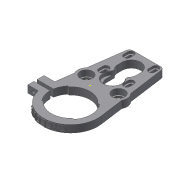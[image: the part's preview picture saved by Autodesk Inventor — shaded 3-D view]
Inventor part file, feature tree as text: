
AUTODESK INVENTOR PART (.ipt)
format: ipt  version: 2015 SP2 (Build 190223200, 223)  size: 483,840 bytes
history: native  units: mm
features: sketch x10, extrude x8, other x3, projected_geometry x3, plane x2, hole x1, pattern_linear x1, chamfer x1
ambient origin geometry x8: Origin, YZ Plane, XZ Plane, XY Plane, X Axis, Y Axis, Z Axis, Center Point
bodies: Body1 (feature_tree)
feature tree (29):
  other  "Sólido1"
  extrude  "Extrusión1"  Depth=15.45mm
  extrude  "Extrusión4"  Depth=12.0mm
  extrude  "Extrusión5"  Depth=40.0mm
  extrude  "Extrusión6"  Depth=10.0mm TaperAngle=0.0deg
  hole  "Agujero1"  [1 undecoded]
  extrude  "Extrusión8"  Depth=48.0mm
  extrude  "Extrusión10"  Depth=6.0mm
  pattern_linear  "Patrón rectangular1"  Spacing1=2.8mm  [1 undecoded]
  extrude  "Extrusión11"  Depth=1.850001mm
  sketch  "Boceto15"  dims[d29=10.0mm d30=0.0mm]
  extrude  "Extrusión12"  Depth=1.850001mm
  plane  "Plano de trabajo1"
  chamfer  "Chaflán1"  Distance=5.0mm
  plane  "Plano de trabajo6"
  sketch  "Boceto27"  dims[d43=6.235mm d44=2.8mm d45=0.0mm d46=1.850001mm d47=1.850001mm d51=5.0mm d52=5.0mm d54=34.5mm d59=5.0mm d60=5.0mm d61=1.85mm d62=15.5mm d63=4.5mm d64=9.0mm d65=0.0mm d66=20.0mm d68=31.0mm d69=20.0mm d71=31.0mm d72=8.200001mm d74=47.65mm d75=2.35mm d76=2.35mm d77=2.35mm d78=2.35mm d79=25.436099mm d80=25.436099mm d81=2.0mm d82=2.0mm d83=2.0mm d84=2.0mm d85=2.8mm d86=0.0mm d89=22.5mm d90=4.5mm d91=0.0mm d92=0.5mm d93=2.0mm d94=30.0deg d95=40.247076mm d99=0.9mm d100=0.0mm]
  other  "Eje de trabajo1"
  other  "Repujado2"
  sketch  "Boceto1"  dims[d0=9.0mm d1=0.0mm d2=15.45mm]
  projected_geometry  "Contorno proyectado1"
  sketch  "Boceto5"  dims[d3=15.45mm d14=12.0mm]
  sketch  "Boceto7"  dims[d15=12.0mm d16=40.0mm]
  projected_geometry  "Contorno proyectado3"
  sketch  "Boceto10"  dims[d19=40.0mm d20=10.0mm d21=0.0mm]
  sketch  "Boceto11"  dims[d22=12.0mm d23=12.0mm]
  sketch  "Boceto12"  dims[d24=2.0mm d25=0.0mm d26=48.0mm]
  sketch  "Boceto13"  dims[d27=30.0mm d28=6.0mm]
  projected_geometry  "Contorno proyectado5"
  sketch  "Boceto16"  dims[d36=3.75mm d37=6.0mm d38=4.0mm d39=2.0mm d40=90.0deg d41=8.0mm d42=20.594885mm]
note: 2 required parameter values undecoded (feature->parameter linkage not recoverable at this tier; creation-order binding heuristic only, values carry confidence <= 0.55)
